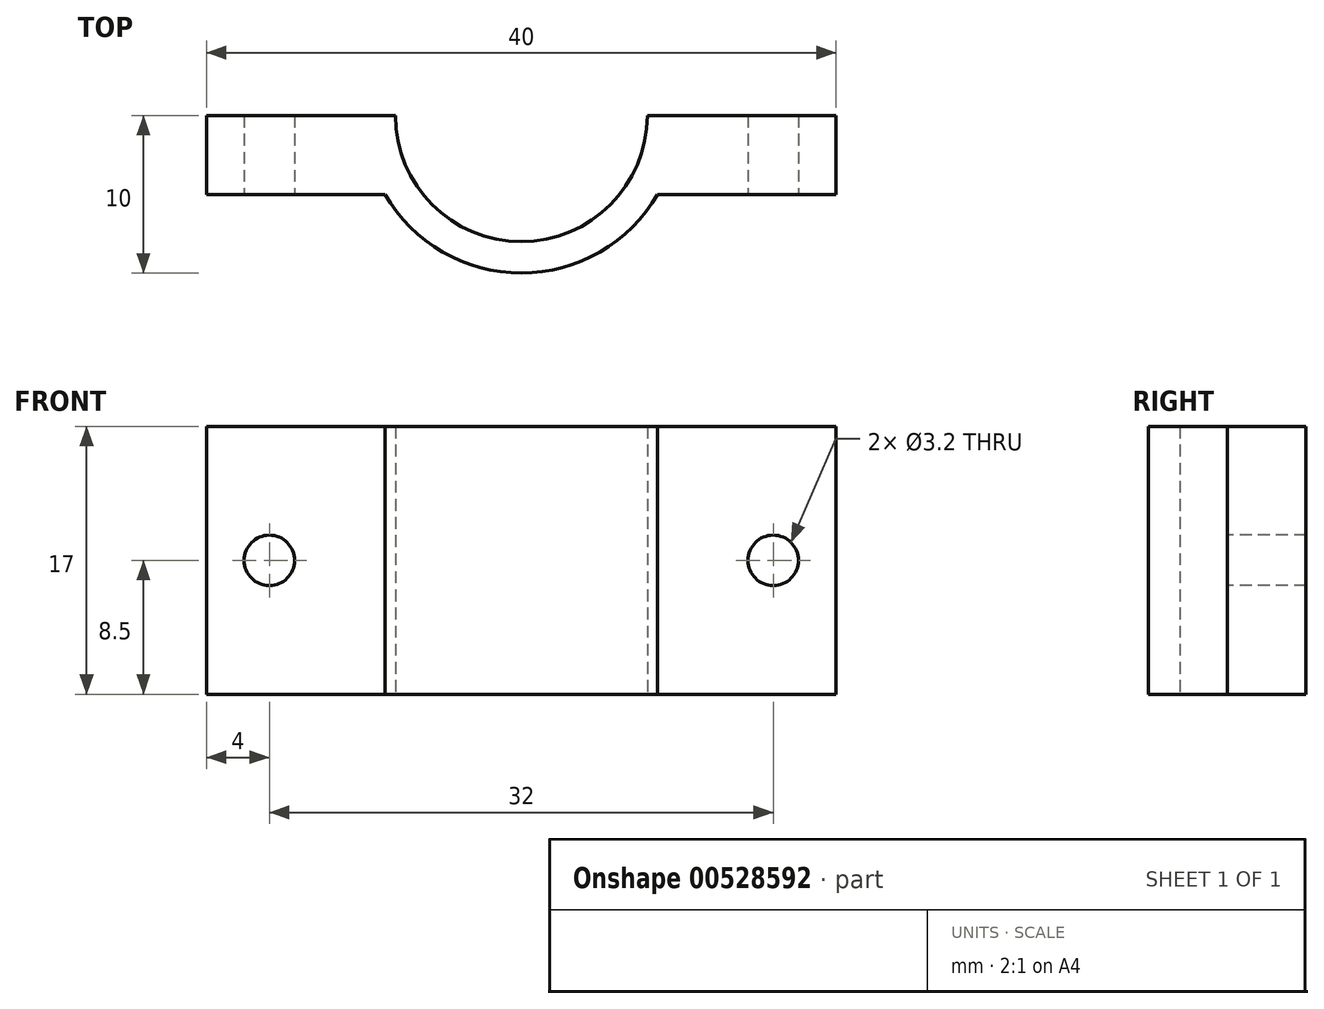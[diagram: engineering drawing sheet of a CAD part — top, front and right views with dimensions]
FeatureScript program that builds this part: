
annotation { "Feature Type Name" : "Feature", "Feature Type Description" : "" }
export const myFeature = defineFeature(function(context is Context, id is Id, definition is map)
    precondition{}
    {
        {
            var Q0;
            Q0=qCreatedBy(makeId("Top.planeOp"),FACE);
            var sketch = newSketch(context, id + "F0", { "sketchPlane" : qUnion([Q0])});
            skLineSegment(sketch, "E0.bottom", {"start": v(-20, 5) * mm, "end": v(-8, 5) * mm});
            skLineSegment(sketch, "E0.top", {"start": v(-20, -5) * mm, "end": v(20, -5) * mm});
            skLineSegment(sketch, "E0.left", {"start": v(-20, 5) * mm, "end": v(-20, -5) * mm});
            skLineSegment(sketch, "E0.right", {"start": v(20, 5) * mm, "end": v(20, -5) * mm});
            skPoint(sketch, "E0.middle", {"position": v(0, 0) * mm});
            skArc(sketch, "E1", {"start": v(-8, 5) * mm, "mid": v(0, -3) * mm, "end": v(8, 5) * mm});
            skLineSegment(sketch, "E2.trimOffspring", {"start": v(8, 5) * mm, "end": v(20, 5) * mm});
            skSolve(sketch);
        }
        {
            var Q0;
            Q0=makeQuery(id+"F0.imprint","IMPRINT",FACE,{"disambiguationData":[TD([[makeQuery(id+"F0.imprint","IMPRINT",EDGE,{"derivedFrom":sQuery(id+"F0.wireOp",EDGE,"E0.bottom")}),-1.0]])]});
            extrude(context, id + "F1", {"entities" : qUnion([Q0]), "depth" : 17 * mm, "offsetDistance" : 25 * mm});
        }
        {
            var Q0;
            Q0=makeQuery(id+"F1.opExtrude","SWEPT_FACE",FACE,{"disambiguationData":[OSD([sQuery(id+"F0.wireOp",EDGE,"E0.top")])]});
            var sketch = newSketch(context, id + "F2", { "sketchPlane" : qUnion([Q0])});
            skCircle(sketch, "E3", {"center": v(-16, 8.5) * mm, "radius": 1.6 * mm});
            skPoint(sketch, "E3.centerSnap0", {"position": v(-20, 8.5) * mm});
            skCircle(sketch, "E4", {"center": v(16, 8.5) * mm, "radius": 1.6 * mm});
            skPoint(sketch, "E4.centerSnap0", {"position": v(20, 8.5) * mm});
            skLineSegment(sketch, "E5", {"start": v(-16, 8.5) * mm, "end": v(-20, 8.5) * mm, "construction": true});
            skLineSegment(sketch, "E6", {"start": v(16, 8.5) * mm, "end": v(20, 8.5) * mm, "construction": true});
            skSolve(sketch);
        }
        {
            var Q0;
            Q0 = qSketchRegion(id + "F2", true);
            extrude(context, id + "F3", {"entities" : qUnion([Q0]), "operationType" : NewBodyOperationType.REMOVE, "oppositeDirection" : true, "depth" : 25 * mm, "offsetDistance" : 25 * mm});
        }
        {
            var Q0;
            Q0=makeQuery(id+"F1.opExtrude","CAP_FACE",FACE,{"disambiguationData":[OSD([sQuery(id+"F0.wireOp",EDGE,"E0.bottom"),sQuery(id+"F0.wireOp",EDGE,"E0.top"),sQuery(id+"F0.wireOp",EDGE,"E0.left"),sQuery(id+"F0.wireOp",EDGE,"E0.right"),sQuery(id+"F0.wireOp",EDGE,"E1"),sQuery(id+"F0.wireOp",EDGE,"E2.trimOffspring")])],"isStart":false});
            var sketch = newSketch(context, id + "F4", { "sketchPlane" : qUnion([Q0])});
            skArc(sketch, "E7", {"start": v(-8.66, 0) * mm, "mid": v(0, -5) * mm, "end": v(8.66, 0) * mm});
            skLineSegment(sketch, "E8", {"start": v(-8.66, 0) * mm, "end": v(-20, 0) * mm});
            skLineSegment(sketch, "E9", {"start": v(-20, 0) * mm, "end": v(-20, -5.93) * mm});
            skLineSegment(sketch, "E10", {"start": v(-20, -5.93) * mm, "end": v(20, -5.93) * mm});
            skLineSegment(sketch, "E11", {"start": v(20, -5.93) * mm, "end": v(20, 0) * mm});
            skLineSegment(sketch, "E12", {"start": v(20, 0) * mm, "end": v(8.66, 0) * mm});
            skSolve(sketch);
        }
        {
            var Q0;
            Q0 = qSketchRegion(id + "F4", true);
            extrude(context, id + "F5", {"entities" : qUnion([Q0]), "operationType" : NewBodyOperationType.REMOVE, "oppositeDirection" : true, "depth" : 25 * mm, "offsetDistance" : 25 * mm});
        }
    });
